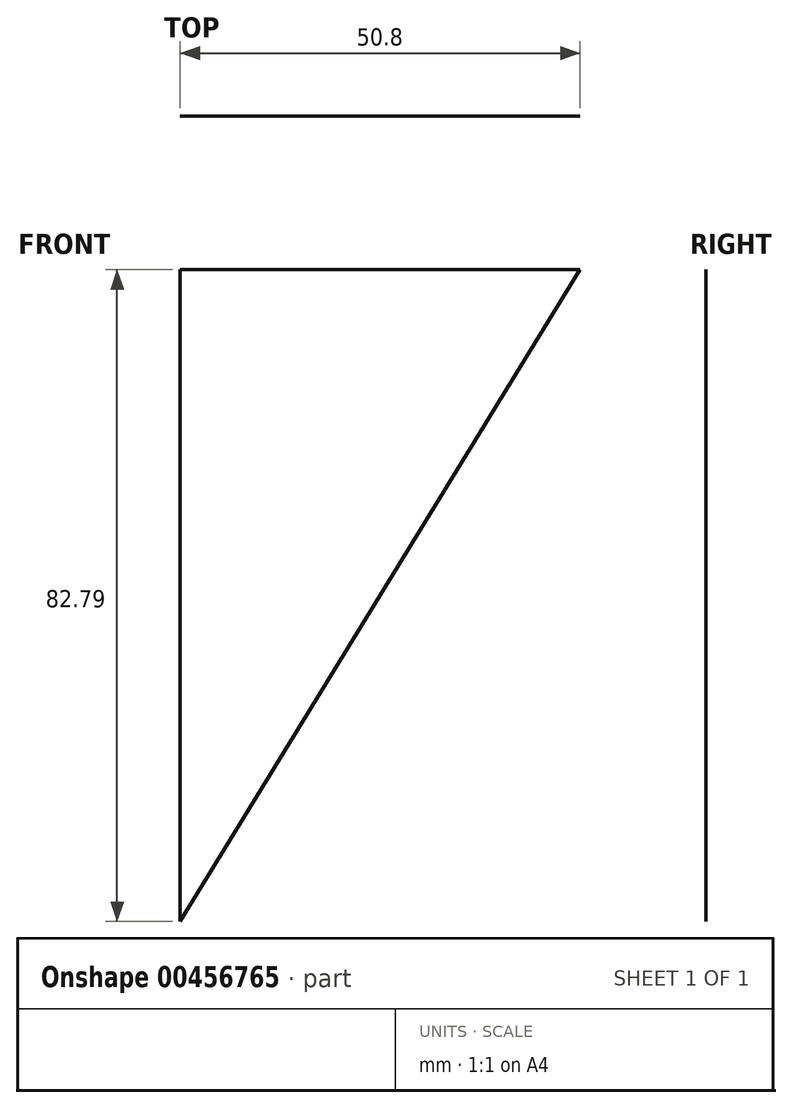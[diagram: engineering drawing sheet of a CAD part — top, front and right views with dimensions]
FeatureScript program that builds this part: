
annotation { "Feature Type Name" : "Feature", "Feature Type Description" : "" }
export const myFeature = defineFeature(function(context is Context, id is Id, definition is map)
    precondition{}
    {
        {
            var Q0;
            Q0=qCreatedBy(makeId("Front.planeOp"),FACE);
            var sketch = newSketch(context, id + "F0", { "sketchPlane" : qUnion([Q0])});
            skLineSegment(sketch, "E0", {"start": v(0, 0) * mm, "end": v(0, -82.8) * mm});
            skLineSegment(sketch, "E1", {"start": v(0, 0) * mm, "end": v(50.8, 0) * mm});
            skLineSegment(sketch, "E2", {"start": v(0, -82.8) * mm, "end": v(50.8, 0) * mm});
            skSolve(sketch);
        }
        {
            var Q0;
            Q0=makeQuery(id+"F0.imprint","IMPRINT",FACE,{"disambiguationData":[TD([[makeQuery(id+"F0.imprint","IMPRINT",EDGE,{"derivedFrom":sQuery(id+"F0.wireOp",EDGE,"E0")}),1.0]])]});
            extrude(context, id + "F1", {"entities" : qUnion([Q0]), "depth" : 1 / 203.2 * mm});
        }
    });
